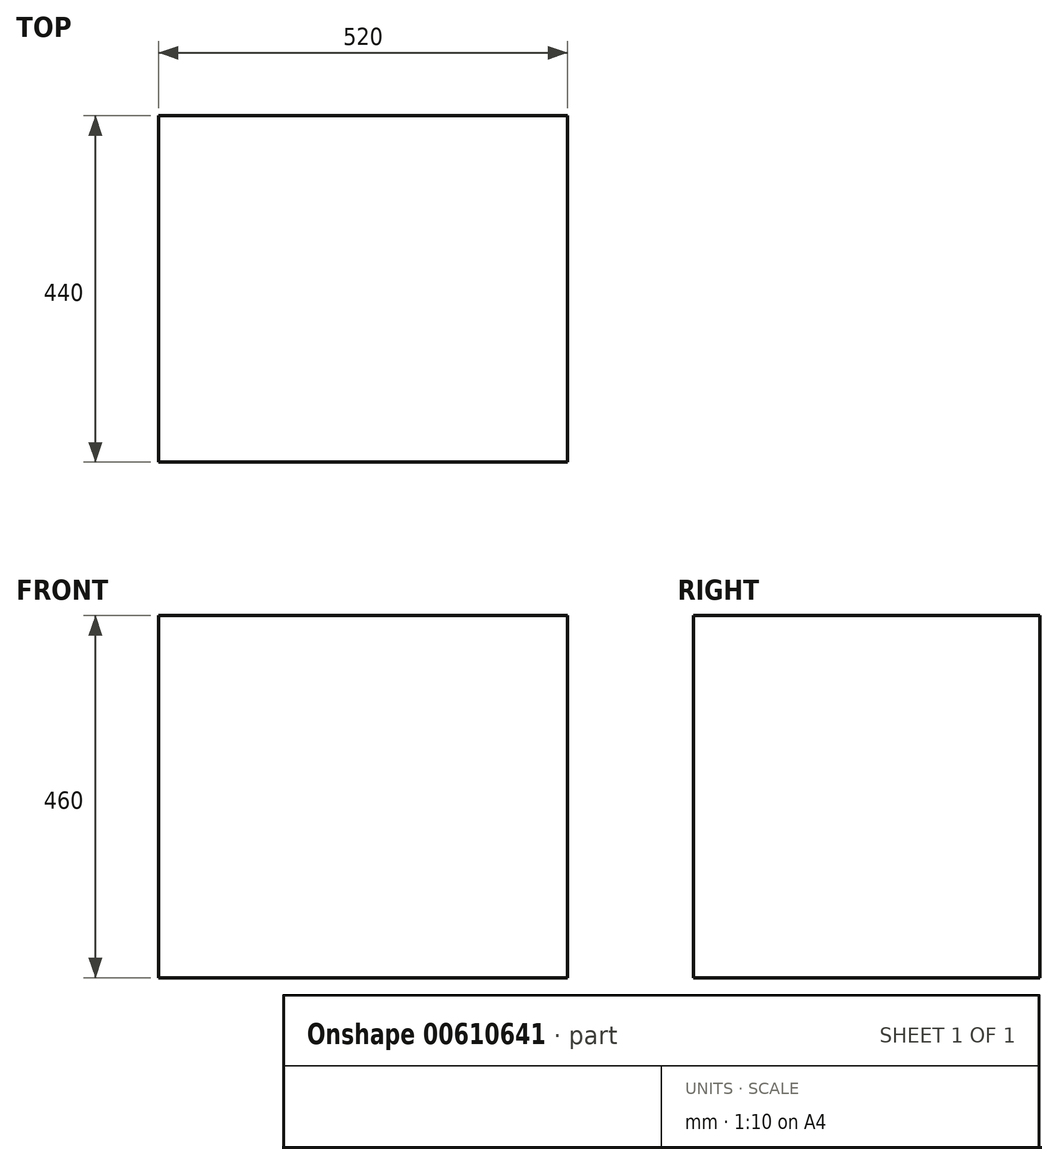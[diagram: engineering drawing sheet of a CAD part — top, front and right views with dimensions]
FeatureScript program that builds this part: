
annotation { "Feature Type Name" : "Feature", "Feature Type Description" : "" }
export const myFeature = defineFeature(function(context is Context, id is Id, definition is map)
    precondition{}
    {
        {
            var Q0;
            Q0=qCreatedBy(makeId("Front.planeOp"),FACE);
            var sketch = newSketch(context, id + "F0", { "sketchPlane" : qUnion([Q0])});
            skLineSegment(sketch, "E0.top", {"start": v(-255, 460) * mm, "end": v(265, 460) * mm});
            skLineSegment(sketch, "E0.left", {"start": v(-255, 0) * mm, "end": v(-255, 460) * mm});
            skLineSegment(sketch, "E0.right", {"start": v(265, 0) * mm, "end": v(265, 460) * mm});
            skPoint(sketch, "E1.endSnap0", {"position": v(5, 460) * mm});
            skLineSegment(sketch, "E2", {"start": v(-255, 0) * mm, "end": v(265, 0) * mm});
            skSolve(sketch);
        }
        {
            var Q0;
            Q0=makeQuery(id+"F0.imprint","IMPRINT",FACE,{"disambiguationData":[TD([[makeQuery(id+"F0.imprint","IMPRINT",EDGE,{"derivedFrom":sQuery(id+"F0.wireOp",EDGE,"E0.top")}),-1.0]])]});
            extrude(context, id + "F1", {"entities" : qUnion([Q0]), "oppositeDirection" : true, "depth" : 440 * mm, "offsetDistance" : 25 * mm});
        }
    });
